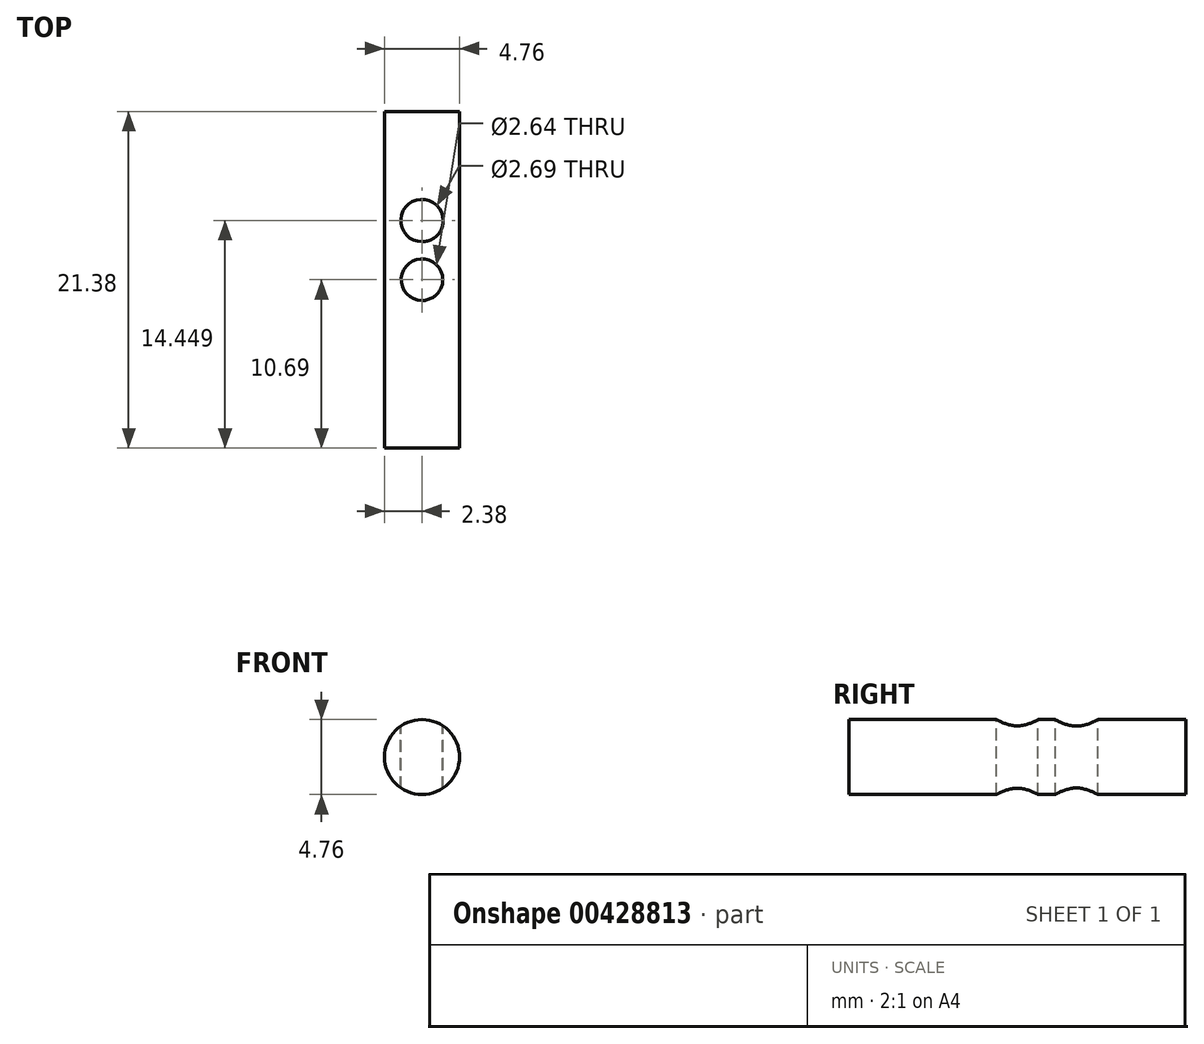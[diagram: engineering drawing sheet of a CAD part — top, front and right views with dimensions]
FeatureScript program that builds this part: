
annotation { "Feature Type Name" : "Feature", "Feature Type Description" : "" }
export const myFeature = defineFeature(function(context is Context, id is Id, definition is map)
    precondition{}
    {
        {
            var Q0;
            Q0=qCreatedBy(makeId("Front.planeOp"),FACE);
            var sketch = newSketch(context, id + "F0", { "sketchPlane" : qUnion([Q0])});
            skCircle(sketch, "E0", {"center": v(0, 0) * mm, "radius": 2.38 * mm});
            skSolve(sketch);
        }
        {
            var Q0;
            Q0 = qSketchRegion(id + "F0", true);
            extrude(context, id + "F1", {"entities" : qUnion([Q0]), "endBound" : BoundingType.SYMMETRIC, "depth" : 21.4 * mm});
        }
        {
            var Q0;
            Q0=qCreatedBy(makeId("Top.planeOp"),FACE);
            cPlane(context, id + "F2", {"entities" : qUnion([Q0]), "cplaneType" : CPlaneType.OFFSET, "offset" : 2.38 * mm, "width" : 152.4 * mm, "height" : 152.4 * mm});
        }
        {
            var Q0;
            Q0=qCreatedBy(id+"F2.planeOp",FACE);
            var sketch = newSketch(context, id + "F3", { "sketchPlane" : qUnion([Q0])});
            skPoint(sketch, "E1", {"position": v(0, 0) * mm});
            skSolve(sketch);
        }
        {
            var Q0;
            Q0=sQuery(id+"F3.wireOp",VERTEX,"E1");
            var Q1;
            Q1=makeQuery(id+"F1.opExtrude","SWEPT_BODY",BODY,{"disambiguationData":[OSD([sQuery(id+"F0.wireOp",EDGE,"E0")])]});
            hole(context, id + "F4", {"style" : HoleStyle.SIMPLE, "endStyle" : HoleEndStyle.THROUGH, "standardTappedOrClearance" : lookupTablePath({ "standard" : "ANSI", "engagement" : "75%", "pitch" : "44 tpi", "size" : "#5", "type" : "Tapped" }), "standardBlindInLast" : lookupTablePath({ "standard" : "ANSI", "engagement" : "75%", "pitch" : "44 tpi", "size" : "#5", "type" : "Tapped" }), "holeDiameter" : 2.64 * mm, "showTappedDepth" : true, "isTappedThrough" : true, "tappedDepth" : 12.7 * mm, "tapClearance" : 3, "startFromSketch" : true, "locations" : qUnion([Q0]), "scope" : qUnion([Q1]), "majorDiameter" : 3.18 * mm});
        }
        {
            var Q0;
            Q0=qCreatedBy(id+"F2.planeOp",FACE);
            var sketch = newSketch(context, id + "F5", { "sketchPlane" : qUnion([Q0])});
            skPoint(sketch, "E2", {"position": v(0, 3.76) * mm});
            skSolve(sketch);
        }
        {
            var Q0;
            Q0=sQuery(id+"F5.wireOp",VERTEX,"E2");
            var Q1;
            Q1=makeQuery(id+"F1.opExtrude","SWEPT_BODY",BODY,{"disambiguationData":[OSD([sQuery(id+"F0.wireOp",EDGE,"E0")])]});
            hole(context, id + "F6", {"style" : HoleStyle.SIMPLE, "endStyle" : HoleEndStyle.THROUGH, "holeDiameter" : 2.7 * mm, "isTappedThrough" : true, "tappedDepth" : 12.7 * mm, "tapClearance" : 3, "startFromSketch" : true, "locations" : qUnion([Q0]), "scope" : qUnion([Q1])});
        }
    });
